# Revit family: Downlight - Recessed Can
name_source: partatom
category: Lighting Fixtures
revit_build: Autodesk Revit Architecture 2012 (Build: 20110210_1515)
units: mm (PartAtom-declared; Revit-internal decimal feet)

## types (6) — shared parameters
Ballast Number of Poles = 1
Color Filter = 16777215
Dimming Lamp Color Temperature Shift = <None>
Load Classification = Lighting - Dwelling Unit
Material = <By Category>
Recessing Height = 0' - 8"
Spot Beam Angle = 30.00°
Spot Field Angle = 90.00°
Tilt Angle = 90.00°

## per-type parameters (varying)
| type | Apparent Load | Assembly Code | Ballast Voltage | Lamp | Light Source Symbol Length | Recessing Diameter | Recessing Inner Radius | Recessing Radius |
| 6" Incandescent - 120V | 60 VA | D5020220 | 120 V | A-19 | 10' - 0" | 0' - 6" | 0' - 2 1/2" | 0' - 3" |
| 8" Incandescent - 120V | 100 VA | D5020220 | 120 V | A-19 | 10' - 0" | 0' - 8" | 0' - 3 1/2" | 0' - 4" |
| 6" Incandescent - 277V | 60 VA | D5020220 | 277 V | A-19 | 10' - 0" | 0' - 6" | 0' - 2 1/2" | 0' - 3" |
| 8" Incandescent - 277V | 100 VA | D5020220 | 277 V | A-19 | 10' - 0" | 0' - 8" | 0' - 3 1/2" | 0' - 4" |
| Fluorescent - 120V | 18 VA | D5020210 | 120 V |  | 10' - 0" | 0' - 8" | 0' - 3 1/2" | 0' - 4" |
| Fluorescent - 277V | 18 VA | D5020210 | 277 V |  | 4' - 0" | 0' - 8" | 0' - 3 1/2" | 0' - 4" |

## geometry (parser evidence)
native form markers: Sweep x1
no freeform markers — native parametric forms only
